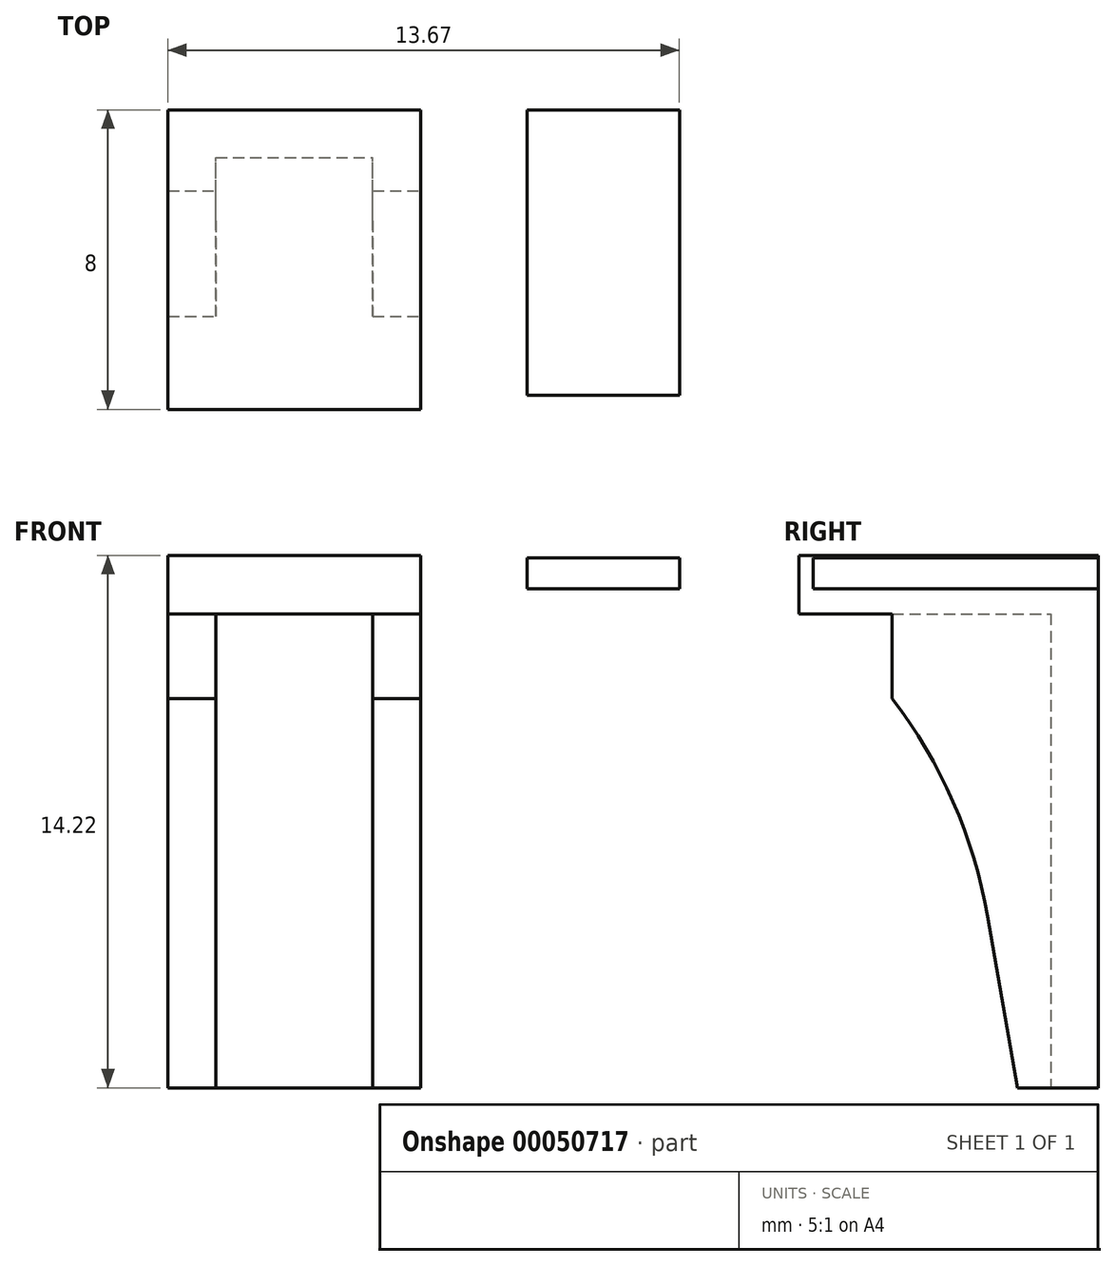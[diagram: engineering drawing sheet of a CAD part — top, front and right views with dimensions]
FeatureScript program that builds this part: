
annotation { "Feature Type Name" : "Feature", "Feature Type Description" : "" }
export const myFeature = defineFeature(function(context is Context, id is Id, definition is map)
    precondition{}
    {
        {
            var Q0;
            Q0=qCreatedBy(makeId("Front.planeOp"),FACE);
            var sketch = newSketch(context, id + "F0", { "sketchPlane" : qUnion([Q0])});
            skLineSegment(sketch, "E0.MirrorCS", {"start": v(0, 0) * mm, "end": v(0, -7.11) * mm});
            skLineSegment(sketch, "E1", {"start": v(-3.38, 7.11) * mm, "end": v(-3.38, -7.11) * mm});
            skLineSegment(sketch, "E2", {"start": v(-3.38, -7.11) * mm, "end": v(3.38, -7.11) * mm});
            skLineSegment(sketch, "E3", {"start": v(3.38, -7.11) * mm, "end": v(3.38, 7.11) * mm});
            skLineSegment(sketch, "E4", {"start": v(-3.38, 7.11) * mm, "end": v(3.38, 7.11) * mm});
            skLineSegment(sketch, "E5", {"start": v(3.38, 7.11) * mm, "end": v(3.38, 5.55) * mm});
            skLineSegment(sketch, "E6", {"start": v(3.38, 5.55) * mm, "end": v(-3.38, 5.55) * mm});
            skLineSegment(sketch, "E7", {"start": v(-3.38, 5.55) * mm, "end": v(-3.38, 7.11) * mm});
            skLineSegment(sketch, "E8", {"start": v(-3.38, 5.55) * mm, "end": v(-2.1, 5.55) * mm});
            skLineSegment(sketch, "E9", {"start": v(-2.1, 5.55) * mm, "end": v(-2.1, -7.11) * mm});
            skLineSegment(sketch, "E10.MirrorCS", {"start": v(2.1, 5.55) * mm, "end": v(2.1, -7.11) * mm});
            skSolve(sketch);
        }
        {
            var Q0;
            Q0=makeQuery(id+"F0.imprint","IMPRINT",FACE,{"disambiguationData":[TD([[makeQuery(id+"F0.imprint","IMPRINT",EDGE,{"derivedFrom":sQuery(id+"F0.wireOp",EDGE,"E4")}),-1.0]])]});
            extrude(context, id + "F1", {"entities" : qUnion([Q0]), "depth" : 8 * mm});
        }
        {
            var Q0;
            {var subQ0=sQuery(id+"F0.wireOp",EDGE,"E1");Q0=makeQuery(id+"F0.imprint","IMPRINT",FACE,{"disambiguationData":[TD([[makeQuery(id+"F0.imprint","IMPRINT",EDGE,{"derivedFrom":subQ0}),1.0]])]});}
            var Q1;
            {var subQ0=sQuery(id+"F0.wireOp",EDGE,"E3");Q1=makeQuery(id+"F0.imprint","IMPRINT",FACE,{"disambiguationData":[TD([[makeQuery(id+"F0.imprint","IMPRINT",EDGE,{"derivedFrom":subQ0}),1.0]])]});}
            extrude(context, id + "F2", {"entities" : qUnion([Q0, Q1]), "operationType" : NewBodyOperationType.ADD, "depth" : 5.5 * mm});
        }
        {
            var Q0;
            {var subQ0=sQuery(id+"F0.wireOp",EDGE,"E9");Q0=makeQuery(id+"F0.imprint","IMPRINT",FACE,{"disambiguationData":[TD([[makeQuery(id+"F0.imprint","IMPRINT",EDGE,{"derivedFrom":subQ0}),1.0]])]});}
            extrude(context, id + "F3", {"entities" : qUnion([Q0]), "operationType" : NewBodyOperationType.ADD, "depth" : 1.27 * mm});
        }
        {
            var Q0;
            Q0=makeQuery(id+"F2.boolean.opBoolean","MERGE",FACE,{"derivedFrom":[makeQuery(id+"F1.opExtrude","SWEPT_FACE",FACE,{"disambiguationData":[OSD([sQuery(id+"F0.wireOp",EDGE,"E5")])]}),makeQuery(id+"F2.opExtrude","SWEPT_FACE",FACE,{"disambiguationData":[OSD([sQuery(id+"F0.wireOp",EDGE,"E3")])]})]});
            var sketch = newSketch(context, id + "F4", { "sketchPlane" : qUnion([Q0])});
            skLineSegment(sketch, "E11", {"start": v(0, -7.11) * mm, "end": v(-2.16, -7.11) * mm});
            skLineSegment(sketch, "E12", {"start": v(-5.51, 5.55) * mm, "end": v(-5.51, 3.29) * mm});
            skLineSegment(sketch, "E13", {"start": v(0, -7.11) * mm, "end": v(0, -2.53) * mm});
            skLineSegment(sketch, "E14", {"start": v(-2.96, -2.53) * mm, "end": v(-2.16, -7.11) * mm});
            skArc(sketch, "E15", {"start": v(-2.96, -2.53) * mm, "mid": v(-3.88, 0.53) * mm, "end": v(-5.51, 3.29) * mm});
            skSolve(sketch);
        }
        {
            var Q0;
            Q0 = qSketchRegion(id + "F4", true);
            var Q1;
            {var subQ0=sQuery(id+"F4.wireOp",EDGE,"E14");Q1=makeQuery(id+"F4.imprint","IMPRINT",FACE,{"disambiguationData":[TD([[makeQuery(id+"F4.imprint","IMPRINT",EDGE,{"derivedFrom":subQ0}),-1.0]])]});}
            extrude(context, id + "F5", {"entities" : qUnion([Q0, Q1]), "operationType" : NewBodyOperationType.REMOVE, "oppositeDirection" : true, "depth" : 25.4 * mm});
        }
        {
            var Q0;
            Q0=qCreatedBy(makeId("Front.planeOp"),FACE);
            var sketch = newSketch(context, id + "F6", { "sketchPlane" : qUnion([Q0])});
            skLineSegment(sketch, "E16", {"start": v(6.22, 7.04) * mm, "end": v(10.3, 7.04) * mm});
            skLineSegment(sketch, "E17", {"start": v(10.3, 7.04) * mm, "end": v(10.3, 6.22) * mm});
            skLineSegment(sketch, "E18", {"start": v(10.3, 6.22) * mm, "end": v(6.22, 6.22) * mm});
            skLineSegment(sketch, "E19", {"start": v(6.22, 6.22) * mm, "end": v(6.22, 7.04) * mm});
            skSolve(sketch);
        }
        {
            var Q0;
            Q0 = qSketchRegion(id + "F6", true);
            extrude(context, id + "F7", {"entities" : qUnion([Q0]), "depth" : 7.62 * mm});
        }
    });
